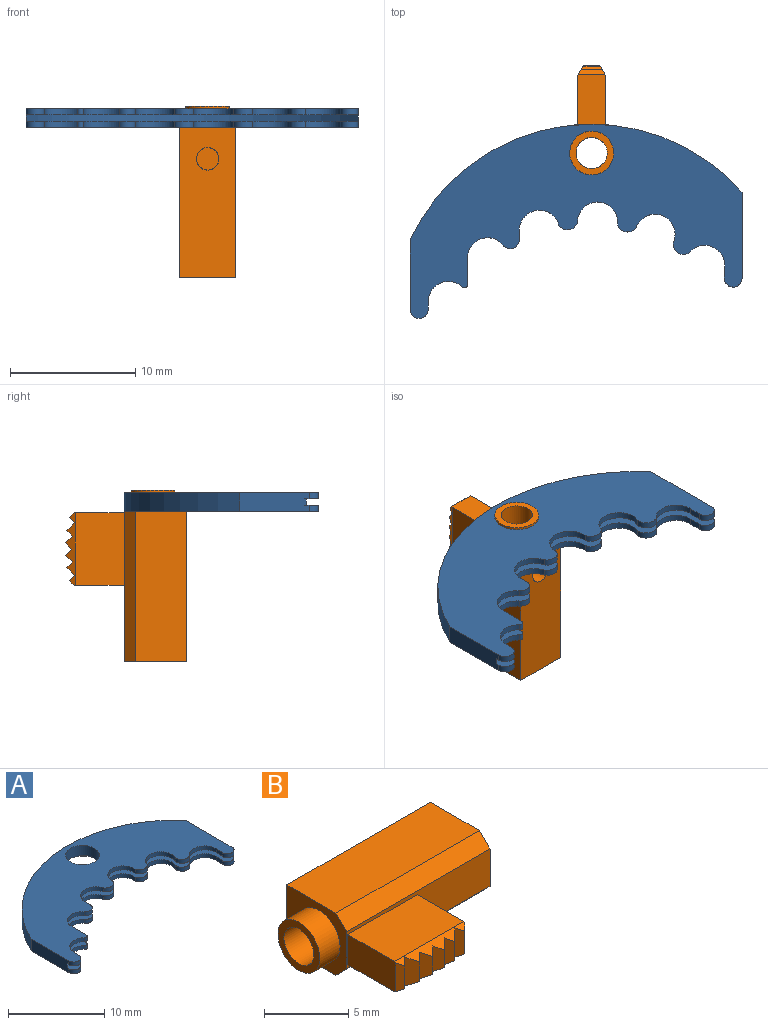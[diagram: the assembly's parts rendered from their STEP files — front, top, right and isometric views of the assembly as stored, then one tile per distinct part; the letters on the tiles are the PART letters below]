
ASSEMBLY  parts=2 mates=1
PART A: 44 faces, bbox 26.5x15.5x1.5 mm
  f0: cylinder r=1.6mm len=3.2mm, axis (0,0,-1), area 2.6mm2, adj f1,f18,f39,f42
  f1: cylinder r=0.83mm len=1.48mm, axis (0,0,-1), area 0.9mm2, adj f0,f2,f39,f42
  f2: cylinder r=1.6mm len=3.12mm, axis (0,0,-1), area 2.6mm2, adj f1,f3,f39,f42
  f3: cylinder r=0.83mm len=1.29mm, axis (0,0,-1), area 0.9mm2, adj f2,f4,f39,f42
  f4: cylinder r=1.6mm len=2.85mm, axis (0,0,-1), area 2mm2, adj f3,f5,f39,f42
  f5: plane 0.96x0.5mm, normal (-1,0.03,0), area 0.5mm2, adj f4,f6,f39,f42
  f6: cylinder r=0.7mm len=1.4mm, axis (0,0,-1), area 1.1mm2, adj f5,f7,f39,f42
  f7: plane 6.88x1.5mm, normal (1,0,0), area 9.5mm2, adj f6,f25,f26,f38,f39,f41,f42,f43
  f8: plane 5.54x1.5mm, normal (-1,0,0), area 8.2mm2, adj f9,f26,f27,f38,f39,f41,f42,f43
  f9: cylinder r=0.73mm len=1.45mm, axis (0,0,-1), area 1.1mm2, adj f8,f10,f39,f42
  f10: plane 0.63x0.5mm, normal (1,0,0), area 0.3mm2, adj f9,f11,f39,f42
  f11: cylinder r=1.6mm len=2.7mm, axis (0,0,-1), area 1.9mm2, adj f10,f12,f39,f42
  f12: cylinder r=0.26mm len=0.5mm, axis (0,0,-1), area 0.3mm2, adj f11,f13,f39,f42
  f13: plane 2.13x0.5mm, normal (1,0,0), area 1.1mm2, adj f12,f14,f39,f42
  f14: cylinder r=1.6mm len=2.85mm, axis (0,0,-1), area 2mm2, adj f13,f15,f39,f42
  f15: cylinder r=0.72mm len=1.29mm, axis (0,0,-1), area 0.9mm2, adj f14,f16,f39,f42
  f16: plane 0.75x0.5mm, normal (1,0,0), area 0.4mm2, adj f15,f17,f39,f42
  f17: cylinder r=1.6mm len=3.15mm, axis (0,0,-1), area 2.3mm2, adj f16,f18,f39,f42
  f18: cylinder r=0.83mm len=1.5mm, axis (0,0,-1), area 0.9mm2, adj f0,f17,f39,f42
  f19: cylinder r=1.6mm len=3.2mm, axis (0,0,-1), area 2.6mm2, adj f20,f36,f38,f43
  f20: cylinder r=0.83mm len=1.48mm, axis (0,0,-1), area 0.9mm2, adj f19,f21,f38,f43
  f21: cylinder r=1.6mm len=3.12mm, axis (0,0,-1), area 2.6mm2, adj f20,f22,f38,f43
  f22: cylinder r=0.83mm len=1.29mm, axis (0,0,-1), area 0.9mm2, adj f21,f23,f38,f43
  f23: cylinder r=1.6mm len=2.85mm, axis (0,0,-1), area 2mm2, adj f22,f24,f38,f43
  f24: plane 0.96x0.5mm, normal (-1,0.03,0), area 0.5mm2, adj f23,f25,f38,f43
  f25: cylinder r=0.7mm len=1.4mm, axis (0,0,-1), area 1.1mm2, adj f7,f24,f38,f43
  f26: cylinder r=16mm len=26.5mm, axis (0,0,-1), area 47.6mm2, adj f7,f8,f38,f39
  f27: cylinder r=0.73mm len=1.45mm, axis (0,0,-1), area 1.1mm2, adj f8,f28,f38,f43
  f28: plane 0.63x0.5mm, normal (1,0,0), area 0.3mm2, adj f27,f29,f38,f43
  f29: cylinder r=1.6mm len=2.7mm, axis (0,0,-1), area 1.9mm2, adj f28,f30,f38,f43
  f30: cylinder r=0.26mm len=0.5mm, axis (0,0,-1), area 0.3mm2, adj f29,f31,f38,f43
  f31: plane 2.13x0.5mm, normal (1,0,0), area 1.1mm2, adj f30,f32,f38,f43
  f32: cylinder r=1.6mm len=2.85mm, axis (0,0,-1), area 2mm2, adj f31,f33,f38,f43
  f33: cylinder r=0.72mm len=1.29mm, axis (0,0,-1), area 0.9mm2, adj f32,f34,f38,f43
  f34: plane 0.75x0.5mm, normal (1,0,0), area 0.4mm2, adj f33,f35,f38,f43
  f35: cylinder r=1.6mm len=3.15mm, axis (0,0,-1), area 2.3mm2, adj f34,f36,f38,f43
  f36: cylinder r=0.83mm len=1.5mm, axis (0,0,-1), area 0.9mm2, adj f19,f35,f38,f43
  f37: cylinder r=1.75mm len=3.5mm, axis (0,0,-1), area 14.3mm2, adj f38,f40
  f38: plane 26.5x15.5mm, normal (0,0,1), area 183.9mm2, adj f7,f8,f19,f20,f21,f22,f23,f24
  f39: plane 26.5x15.5mm, normal (0,0,-1), area 181.6mm2, adj f0,f1,f2,f3,f4,f5,f6,f7
  f40: cone r=1.95mm half-angle=45deg, axis (0,0,-1), area 3.3mm2, adj f37,f39
  f41: cylinder r=16mm len=26.5mm, axis (0,0,1), area 15.9mm2, adj f7,f8,f42,f43
  f42: plane 26.5x10.2mm, normal (0,0,1), area 53.1mm2, adj f0,f1,f2,f3,f4,f5,f6,f7
  f43: plane 26.5x10.2mm, normal (0,0,-1), area 53.1mm2, adj f7,f8,f19,f20,f21,f22,f23,f24
PART B: 32 faces, bbox 13.7x9.7x4.5 mm
  f0: plane 5.8x3.9mm, normal (0,0,1), area 22.6mm2, adj f2,f3,f16,f25
  f1: plane 5.8x3.9mm, normal (0,0,-1), area 22.6mm2, adj f2,f3,f16,f24
  f2: plane 4x2.2mm, normal (1,0,0), area 8.8mm2, adj f0,f1,f15,f16,f24,f25
  f3: plane 4x2.2mm, normal (-1,0,0), area 8.8mm2, adj f0,f1,f4,f16,f24,f25
  f4: plane 2.09x0.38mm, normal (-0.71,-0.71,0), area 1mm2, adj f3,f5,f24,f25
  f5: plane 2.13x0.41mm, normal (0.71,-0.71,0), area 1.1mm2, adj f4,f6,f24,f25
  f6: plane 2.13x0.63mm, normal (-0.71,-0.71,0), area 1.6mm2, adj f5,f7,f24,f25
  f7: plane 1.92x0.45mm, normal (0.71,-0.71,0), area 1mm2, adj f6,f8,f24,f25
  f8: plane 1.92x0.54mm, normal (-0.71,-0.71,0), area 1.2mm2, adj f7,f9,f24,f25
  f9: plane 1.85x0.49mm, normal (0.71,-0.71,0), area 1.1mm2, adj f8,f10,f24,f25
  f10: plane 1.85x0.49mm, normal (-0.71,-0.71,0), area 1.1mm2, adj f9,f11,f24,f25
  f11: plane 1.92x0.54mm, normal (0.71,-0.71,0), area 1.2mm2, adj f10,f12,f24,f25
  f12: plane 1.92x0.45mm, normal (-0.71,-0.71,0), area 1mm2, adj f11,f13,f24,f25
  f13: plane 2.13x0.63mm, normal (0.71,-0.71,0), area 1.6mm2, adj f12,f14,f24,f25
  f14: plane 2.13x0.41mm, normal (-0.71,-0.71,0), area 1.1mm2, adj f13,f15,f24,f25
  f15: plane 2.09x0.38mm, normal (0.71,-0.71,0), area 1mm2, adj f2,f14,f24,f25
  f16: plane 12x2.7mm, normal (0,-1,0), area 19.6mm2, adj f0,f1,f2,f3,f17,f19,f22,f23
  f17: plane 5x4.5mm, normal (1,0,0), area 16.8mm2, adj f16,f18,f20,f21,f22,f23,f26
  f18: plane 12x4.5mm, normal (0,1,0), area 51.5mm2, adj f17,f19,f20,f21,f31
  f19: plane 5x4.5mm, normal (-1,0,0), area 12.1mm2, adj f16,f18,f20,f21,f22,f23,f27
  f20: plane 12x4.1mm, normal (0,0,1), area 49.2mm2, adj f17,f18,f19,f23
  f21: plane 12x4.1mm, normal (0,0,-1), area 49.2mm2, adj f17,f18,f19,f22
  f22: plane 12x0.9mm, normal (0,-0.71,-0.71), area 15.3mm2, adj f16,f17,f19,f21
  f23: plane 12x0.9mm, normal (0,-0.71,0.71), area 15.3mm2, adj f16,f17,f19,f20
  f24: plane 5.8x0.79mm, normal (0,-0.5,-0.87), area 2.8mm2, adj f1,f2,f3,f4,f5,f6,f7,f8
  f25: plane 5.8x0.79mm, normal (0,-0.5,0.87), area 2.8mm2, adj f0,f2,f3,f4,f5,f6,f7,f8
  f26: cylinder r=1.25mm len=13.7mm, axis (1,0,0), area 102.1mm2, adj f17,f28,f30,f31
  f27: cylinder r=1.75mm len=3.5mm, axis (1,0,0), area 18.7mm2, adj f19,f28
  f28: plane 3.5x3.5mm, normal (-1,0,0), area 4.7mm2, adj f26,f27
  f29: plane 1.8x1.8mm, normal (0,1,0), area 2.5mm2, adj f30
  f30: cylinder r=0.9mm len=4.63mm, axis (0,1,0), area 25.1mm2, adj f26,f29
  f31: cylinder r=0.9mm len=1.83mm, axis (0,1,0), area 9.2mm2, adj f18,f26
PLACE A at identity fixed
PLACE B rot(axis=(-0.71,0,0.71),180deg) t=(0,21.3,-12.75)mm
MATE fastened B.f26 <-> A.f37  axis (0,0,-1) through (0,19,-0.75)mm
